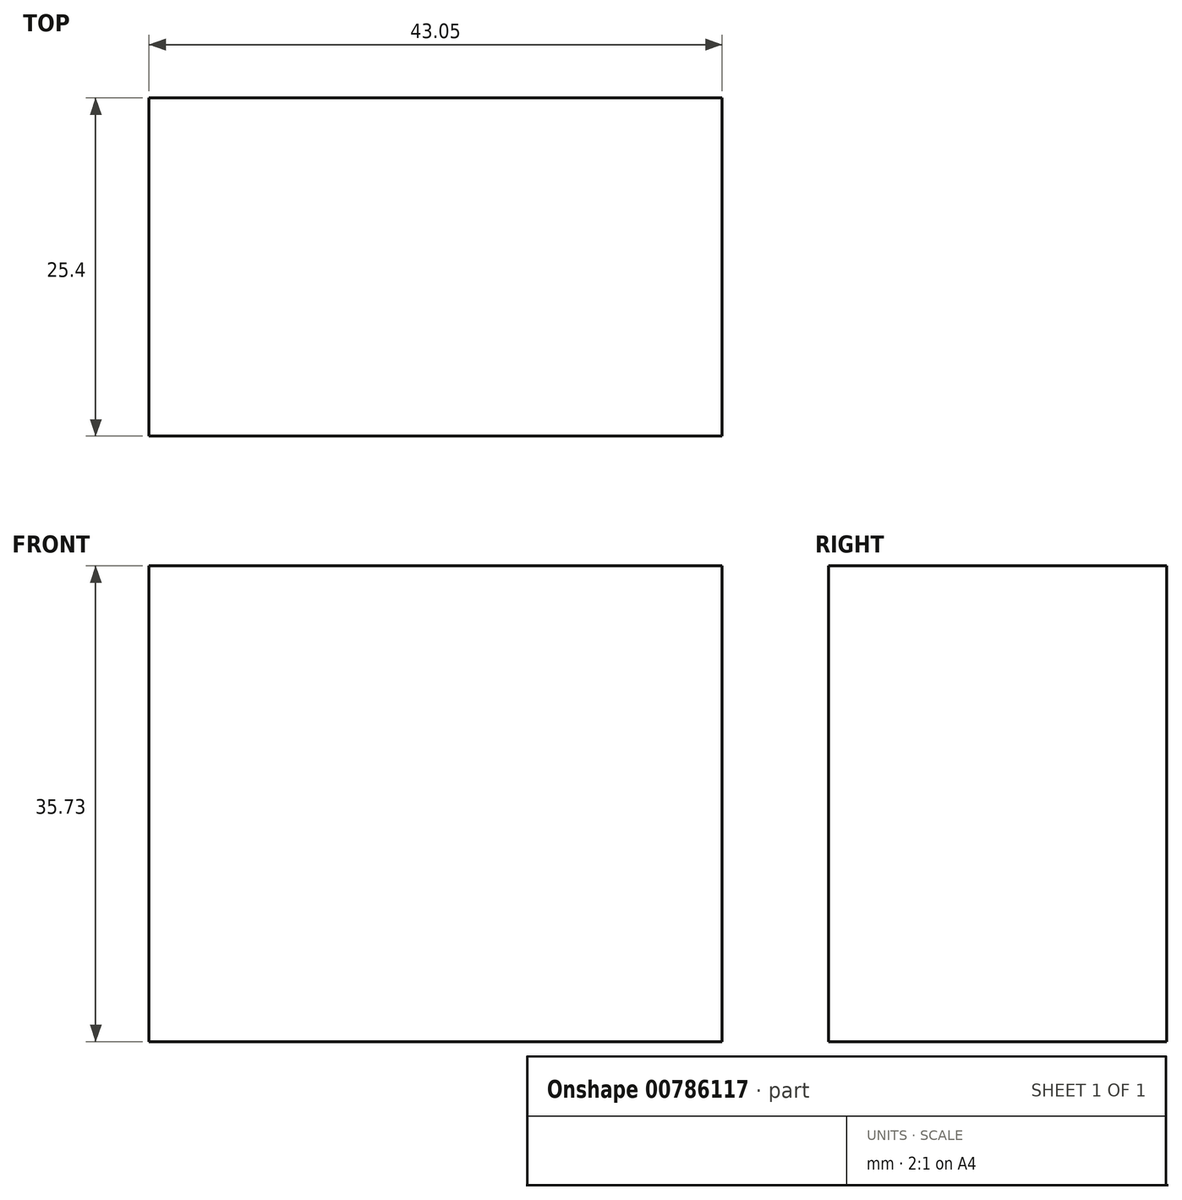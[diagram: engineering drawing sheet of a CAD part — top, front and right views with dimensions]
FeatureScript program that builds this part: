
annotation { "Feature Type Name" : "Feature", "Feature Type Description" : "" }
export const myFeature = defineFeature(function(context is Context, id is Id, definition is map)
    precondition{}
    {
        {
            var Q0;
            Q0=qCreatedBy(makeId("Front.planeOp"),FACE);
            var sketch = newSketch(context, id + "F0", { "sketchPlane" : qUnion([Q0])});
            skLineSegment(sketch, "E0.bottom", {"start": v(-37.1, 8.4) * mm, "end": v(5.95, 8.4) * mm});
            skLineSegment(sketch, "E0.top", {"start": v(-37.1, -27.33) * mm, "end": v(5.95, -27.33) * mm});
            skLineSegment(sketch, "E0.left", {"start": v(-37.1, 8.4) * mm, "end": v(-37.1, -27.33) * mm});
            skLineSegment(sketch, "E0.right", {"start": v(5.95, 8.4) * mm, "end": v(5.95, -27.33) * mm});
            skSolve(sketch);
        }
        {
            var Q0;
            Q0=makeQuery(id+"F0.imprint","IMPRINT",FACE,{"disambiguationData":[TD([[makeQuery(id+"F0.imprint","IMPRINT",EDGE,{"derivedFrom":sQuery(id+"F0.wireOp",EDGE,"E0.bottom")}),-1.0]])]});
            extrude(context, id + "F1", {"entities" : qUnion([Q0]), "depth" : 25.4 * mm, "offsetDistance" : 25.4 * mm});
        }
    });
